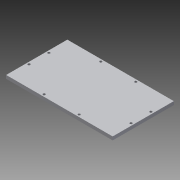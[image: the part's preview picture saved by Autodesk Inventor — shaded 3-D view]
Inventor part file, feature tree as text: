
AUTODESK INVENTOR PART (.ipt)
format: ipt  version: 2015 (Build 190159000, 159)  size: 94,720 bytes
history: native  units: in
note: dims shown in document units (in); Inventor stores cm internally (conversion verified against a paired STEP export)
features: reference x8, extrude x2, sketch x2, fillet x1
ambient origin geometry x8: Origin, YZ Plane, XZ Plane, XY Plane, X Axis, Y Axis, Z Axis, Center Point
bodies: Solid1 (feature_tree)
feature tree (13):
  extrude  "Extrusion1"  Depth=6.75in
  extrude  "Extrusion2"  Depth=0.375in TaperAngle=0.0deg
  fillet  "Fillet1"  Radius=0.125in
  sketch  "Sketch1"  dims[d0=11.75in d1=6.75in]
  sketch  "Sketch3"  dims[d2=0.375in d3=0.0in d25=0.375in d26=0.0in d27=0.125in]
  reference  "Reference1"
  reference  "Reference2"
  reference  "Reference3"
  reference  "Reference4"
  reference  "Reference5"
  reference  "Reference6"
  reference  "Reference7"
  reference  "Reference8"
